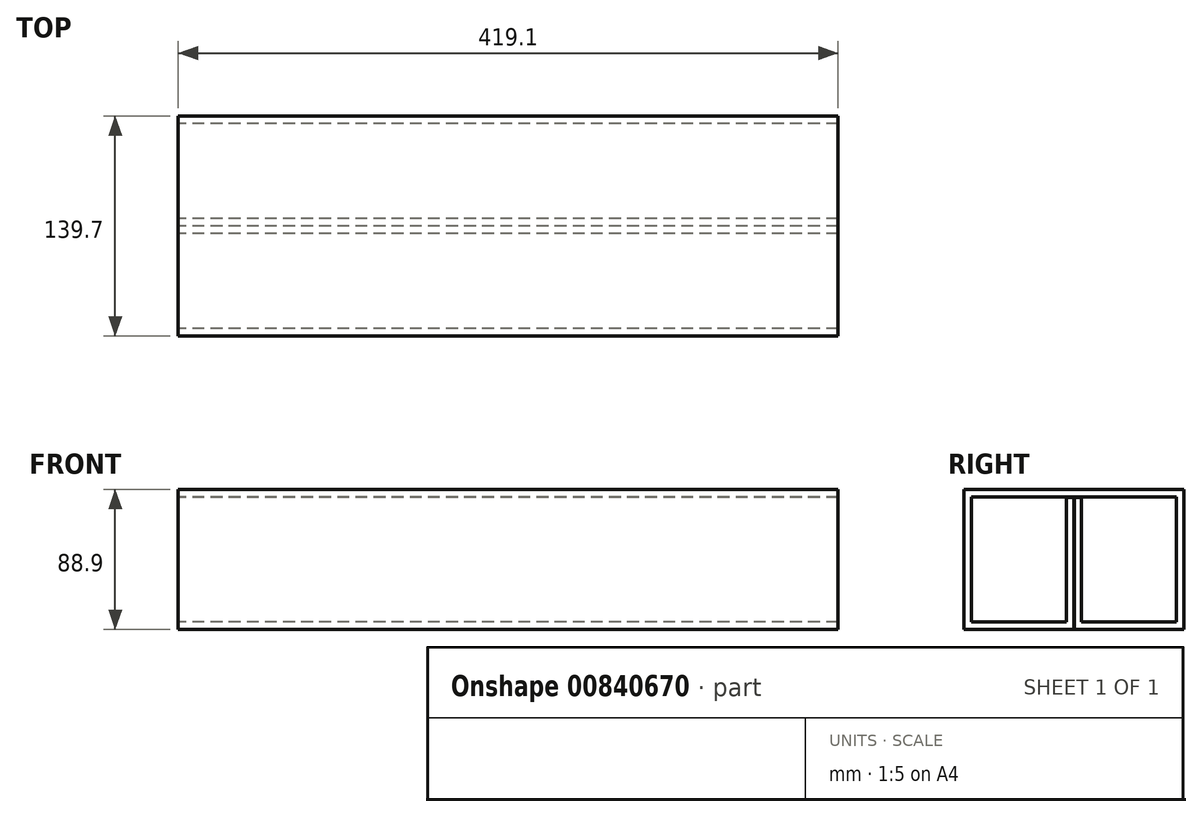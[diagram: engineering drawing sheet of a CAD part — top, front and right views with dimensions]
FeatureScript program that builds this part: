
annotation { "Feature Type Name" : "Feature", "Feature Type Description" : "" }
export const myFeature = defineFeature(function(context is Context, id is Id, definition is map)
    precondition{}
    {
        {
            var Q0;
            Q0=qCreatedBy(makeId("Right.planeOp"),FACE);
            var sketch = newSketch(context, id + "F0", { "sketchPlane" : qUnion([Q0])});
            skLineSegment(sketch, "E0", {"start": v(0, 0) * mm, "end": v(0, 126.35) * mm, "construction": true});
            skLineSegment(sketch, "E1.bottom", {"start": v(-69.85, 88.9) * mm, "end": v(69.85, 88.9) * mm});
            skLineSegment(sketch, "E1.top", {"start": v(-69.85, 0) * mm, "end": v(-0.13, 0) * mm});
            skLineSegment(sketch, "E1.left", {"start": v(-69.85, 88.9) * mm, "end": v(-69.85, 0) * mm});
            skLineSegment(sketch, "E2.0", {"start": v(-65.09, 84.14) * mm, "end": v(65.09, 84.14) * mm});
            skLineSegment(sketch, "E2.1", {"start": v(-65.09, 84.14) * mm, "end": v(-65.09, 4.76) * mm});
            skLineSegment(sketch, "E2.2", {"start": v(-65.09, 4.76) * mm, "end": v(-4.76, 4.76) * mm});
            skLineSegment(sketch, "E2.3", {"start": v(-4.76, 83.88) * mm, "end": v(-4.76, 4.76) * mm});
            skLineSegment(sketch, "E3.MirrorCS", {"start": v(69.85, 88.9) * mm, "end": v(69.85, 0) * mm});
            skLineSegment(sketch, "E4.MirrorCS", {"start": v(4.76, 83.88) * mm, "end": v(4.76, 4.76) * mm});
            skLineSegment(sketch, "E5.MirrorCS", {"start": v(65.09, 4.76) * mm, "end": v(4.76, 4.76) * mm});
            skLineSegment(sketch, "E6.MirrorCS", {"start": v(65.09, 84.14) * mm, "end": v(65.09, 4.76) * mm});
            skLineSegment(sketch, "E7.left", {"start": v(-0.13, 0) * mm, "end": v(-0.13, 83.88) * mm});
            skLineSegment(sketch, "E7.right", {"start": v(0.13, 0) * mm, "end": v(0.13, 83.88) * mm});
            skLineSegment(sketch, "E8.trimOffspring", {"start": v(0.13, 0) * mm, "end": v(69.85, 0) * mm});
            skLineSegment(sketch, "E9", {"start": v(-4.76, 83.88) * mm, "end": v(-0.13, 83.88) * mm});
            skPoint(sketch, "E10.orphan", {"position": v(4.76, 84.14) * mm});
            skLineSegment(sketch, "E11.trimOffspring", {"start": v(0.13, 83.88) * mm, "end": v(4.76, 83.88) * mm});
            skPoint(sketch, "E12.orphan", {"position": v(-4.76, 84.14) * mm});
            skSolve(sketch);
        }
        {
            var Q0;
            Q0 = qSketchRegion(id + "F0", true);
            extrude(context, id + "F1", {"entities" : qUnion([Q0]), "endBound" : BoundingType.SYMMETRIC, "depth" : 419.1 * mm, "offsetDistance" : 25.4 * mm});
        }
    });
